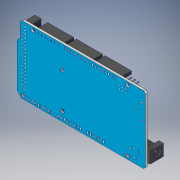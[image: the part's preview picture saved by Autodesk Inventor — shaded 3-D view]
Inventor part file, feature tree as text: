
AUTODESK INVENTOR PART (.ipt)
format: ipt  version: 2019 (Build 230136000, 136)  size: 1,307,136 bytes
history: mixed  units: mm
features: projected_geometry x3, extrude x2, sketch x2, other x1, fillet x1, imported_body x1
ambient origin geometry x8: Origin, YZ Plane, XZ Plane, XY Plane, X Axis, Y Axis, Z Axis, Center Point
bodies: Body1 (imported_parasolid)
feature tree (10):
  other  "Твердое тело1"
  extrude  "Выдавливание1"  Depth=10.0mm TaperAngle=0.0deg
  extrude  "Выдавливание2"  Depth=2.6mm
  sketch  "Эскиз2"
  projected_geometry  "Спроецированная петля1"
  projected_geometry  "Спроецированная петля2"
  projected_geometry  "Спроецированная петля3"
  sketch  "Эскиз3"
  fillet  "Fillet5"  Radius=2.6mm
  imported_body  NMx_Import_Brep_tag  [imported B-rep: ~289 faces, bbox_mm=[103.4288, 53.4162, 12.446]]
